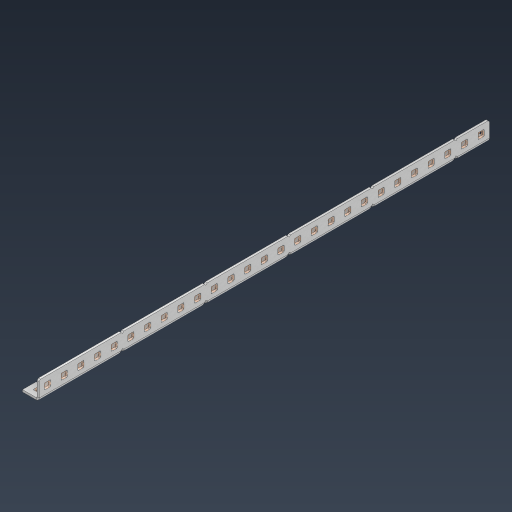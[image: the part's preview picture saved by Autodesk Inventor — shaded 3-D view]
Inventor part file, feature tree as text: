
AUTODESK INVENTOR PART (.ipt)
format: ipt  version: 2024.3 (Build 283343000, 343)  size: 1,052,672 bytes
history: native  units: in
note: dims shown in document units (in); Inventor stores cm internally (conversion verified against a paired STEP export)
features: other x88, extrude x79, sheet_metal_op x11, pattern_linear x2, mirror x1, chamfer x1, sketch x1
ambient origin geometry x8: Origin, YZ Plane, XZ Plane, XY Plane, X Axis, Y Axis, Z Axis, Center Point
bodies: Solid1 (feature_tree), Body (feature_tree)
feature tree (183):
  sheet_metal_op  "Flanges"
  other  "Flange Pattern Plane"
  other  "Flange Pattern Sketch"
  sheet_metal_op  "Flange Pattern"
  sheet_metal_op  "Body Pattern"
  pattern_linear  "Center Pattern"  Spacing1=13.5in  [1 undecoded]
  other  "Arc Length"
  mirror  "Notch Mirror"
  pattern_linear  "Notch Pattern"  Spacing1=0.0625in  [1 undecoded]
  chamfer  "End Chamfer"
  extrude  "Half Cut"  Depth=0.0625in
  other  "Plate1"
  sketch  "Sketch2"  dims[d0=1.0in d1=13.5in d2=0.0625in d3=0.0625in d4=0.0312in d5=0.125in d6=0.0625in d7=0.5in d8=90.0deg d9=0.0312in d10=0.25in d11=0.0625in d12=0.0625in d16=0.182in d17=0.02in d18=0.0625in d19=0.0in d20=0.25in d21=0.25in d38=10.6299in d40=0.5in d41=0.3937in d43=1.0in d46=0.172in d47=1.0in d48=0.0in d49=0.182in d50=0.02in d51=0.25in d52=0.25in d53=0.0625in d54=0.0in d55=0.172in d56=1.0in d57=0.0in d58=0.25in d60=10.6299in d62=0.5in d63=0.3937in d65=0.5in d85=0.1473in d86=0.1782in d88=0.04in d89=0.0625in d90=0.0in d91=0.04in d92=0.0491in d95=2.5in d96=0.04in d97=0.25in d98=45.0deg d99=0.25in d100=0.5in d101=0.0in d102=2.497in d106=0.182in d107=0.02in d108=0.5in d109=0.5in d110=0.0625in d111=0.0in d112=0.172in d113=0.5in d114=0.0in d117=0.5in d118=0.5in d119=0.5in]
  other  "Plate2"
  sheet_metal_op  "Bend1"
  sheet_metal_op  "Corner1"
  other  "Srf1"
  other  "Srf2"
  other  "Srf91"
  sheet_metal_op  "Body Pattern Sketch"
  other  "Srf92"
  other  "Srf786"
  other  "Srf823"
  other  "Srf824"
  other  "Srf825"
  other  "Srf826"
  other  "Srf827"
  other  "Srf828"
  other  "Srf829"
  other  "Srf856"
  other  "Srf857"
  other  "Srf858"
  other  "Srf859"
  other  "Srf860"
  other  "Srf861"
  other  "Srf862"
  other  "Srf889"
  other  "Srf890"
  other  "Srf891"
  other  "Srf892"
  other  "Srf893"
  other  "Srf894"
  other  "Srf895"
  other  "Srf896"
  other  "Srf922"
  other  "Srf923"
  other  "Srf924"
  other  "Srf925"
  other  "Srf926"
  other  "Srf959"
  other  "Srf960"
  other  "Srf961"
  other  "Srf962"
  other  "Srf963"
  other  "Srf996"
  other  "Srf997"
  other  "Srf998"
  other  "Srf999"
  other  "Srf1000"
  other  "Srf1143"
  other  "Srf1144"
  other  "Srf1145"
  other  "Srf1146"
  other  "Srf1147"
  other  "Srf1148"
  other  "Srf1149"
  other  "Srf1150"
  other  "Srf1151"
  other  "Srf1152"
  other  "Srf1153"
  other  "Srf1154"
  other  "Srf1155"
  other  "Srf1199"
  other  "Srf1200"
  other  "Srf1201"
  other  "Srf1202"
  other  "Srf1203"
  other  "Srf1204"
  other  "Srf1205"
  other  "Srf1206"
  other  "Srf1207"
  other  "Srf1208"
  other  "Srf1209"
  other  "Srf1210"
  other  "Srf1211"
  other  "Srf1255"
  other  "Srf1256"
  other  "Srf1257"
  other  "Srf1258"
  other  "Srf1259"
  other  "Srf1260"
  other  "Srf1261"
  other  "Srf1262"
  other  "Srf1263"
  other  "Srf1264"
  other  "Srf1265"
  other  "Srf1266"
  other  "Srf1267"
  sheet_metal_op  "Flange Stamp"
  sheet_metal_op  "Flange Circle"
  sheet_metal_op  "Body Stamp"
  sheet_metal_op  "Body Circle"
  other  "Center Stamp"
  other  "Center Circle"
  sheet_metal_op  "Notch"
  extrude  "ExtrusionSrf2"  Depth=0.0312in
  extrude  "ExtrusionSrf92"  Depth=0.5in
  extrude  "ExtrusionSrf823"  Depth=0.0625in
  extrude  "ExtrusionSrf824"  Depth=0.5in TaperAngle=90.0deg
  extrude  "ExtrusionSrf825"  Depth=0.5in
  extrude  "ExtrusionSrf826"  Depth=0.0625in
  extrude  "ExtrusionSrf827"  Depth=0.0625in
  extrude  "ExtrusionSrf828"  Depth=0.182in
  extrude  "ExtrusionSrf829"  Depth=0.02in
  extrude  "ExtrusionSrf856"  Depth=0.0625in
  extrude  "ExtrusionSrf857"  TaperAngle=0.0deg  [1 undecoded]
  extrude  "ExtrusionSrf858"  Depth=0.5in
  extrude  "ExtrusionSrf859"  Depth=0.5in
  extrude  "ExtrusionSrf860"  Depth=0.5in
  extrude  "ExtrusionSrf861"  Depth=0.5in
  extrude  "ExtrusionSrf862"  Depth=1.0in TaperAngle=0.0deg
  extrude  "ExtrusionSrf889"  Depth=0.182in
  extrude  "ExtrusionSrf890"  Depth=0.02in
  extrude  "ExtrusionSrf891"  Depth=0.5in
  extrude  "ExtrusionSrf892"  Depth=0.5in
  extrude  "ExtrusionSrf893"  Depth=0.0625in
  extrude  "ExtrusionSrf894"  TaperAngle=0.0deg  [1 undecoded]
  extrude  "ExtrusionSrf895"  Depth=0.5in
  extrude  "ExtrusionSrf896"  Depth=1.0in TaperAngle=0.0deg
  extrude  "ExtrusionSrf922"  Depth=0.5in
  extrude  "ExtrusionSrf923"  Depth=0.5in
  extrude  "ExtrusionSrf924"  Depth=0.5in
  extrude  "ExtrusionSrf925"  Depth=0.5in
  extrude  "ExtrusionSrf926"  Depth=0.5in
  extrude  "ExtrusionSrf959"  Depth=0.5in
  extrude  "ExtrusionSrf960"  Depth=0.0625in
  extrude  "ExtrusionSrf961"  TaperAngle=0.0deg  [1 undecoded]
  extrude  "ExtrusionSrf962"  Depth=0.5in
  extrude  "ExtrusionSrf963"  Depth=0.5in
  extrude  "ExtrusionSrf996"  Depth=0.5in
  extrude  "ExtrusionSrf997"  Depth=0.5in TaperAngle=45.0deg
  extrude  "ExtrusionSrf998"  Depth=0.5in
  extrude  "ExtrusionSrf999"  Depth=0.5in TaperAngle=0.0deg
  extrude  "ExtrusionSrf1000"  Depth=0.5in
  extrude  "ExtrusionSrf1143"  Depth=0.182in
  extrude  "ExtrusionSrf1144"  Depth=0.02in
  extrude  "ExtrusionSrf1145"  Depth=0.5in
  extrude  "ExtrusionSrf1146"  Depth=0.5in
  extrude  "ExtrusionSrf1147"  Depth=0.0625in
  extrude  "ExtrusionSrf1148"  TaperAngle=0.0deg  [1 undecoded]
  extrude  "ExtrusionSrf1149"  Depth=0.5in
  extrude  "ExtrusionSrf1150"  Depth=0.5in TaperAngle=0.0deg
  extrude  "ExtrusionSrf1151"  Depth=0.5in
  extrude  "ExtrusionSrf1152"  Depth=0.5in
  extrude  "ExtrusionSrf1153"  Depth=0.5in
  extrude  "ExtrusionSrf1154"  [1 undecoded]
  extrude  "ExtrusionSrf1155"  [1 undecoded]
  extrude  "ExtrusionSrf1199"  [1 undecoded]
  extrude  "ExtrusionSrf1200"  [1 undecoded]
  extrude  "ExtrusionSrf1201"  [1 undecoded]
  extrude  "ExtrusionSrf1202"  [1 undecoded]
  extrude  "ExtrusionSrf1203"  [1 undecoded]
  extrude  "ExtrusionSrf1204"  [1 undecoded]
  extrude  "ExtrusionSrf1205"  [1 undecoded]
  extrude  "ExtrusionSrf1206"  [1 undecoded]
  extrude  "ExtrusionSrf1207"  [1 undecoded]
  extrude  "ExtrusionSrf1208"  [1 undecoded]
  extrude  "ExtrusionSrf1209"  [1 undecoded]
  extrude  "ExtrusionSrf1210"  [1 undecoded]
  extrude  "ExtrusionSrf1211"  [1 undecoded]
  extrude  "ExtrusionSrf1255"  [1 undecoded]
  extrude  "ExtrusionSrf1256"  [1 undecoded]
  extrude  "ExtrusionSrf1257"  [1 undecoded]
  extrude  "ExtrusionSrf1258"  [1 undecoded]
  extrude  "ExtrusionSrf1259"  [1 undecoded]
  extrude  "ExtrusionSrf1260"  [1 undecoded]
  extrude  "ExtrusionSrf1261"  [1 undecoded]
  extrude  "ExtrusionSrf1262"  [1 undecoded]
  extrude  "ExtrusionSrf1263"  [1 undecoded]
  extrude  "ExtrusionSrf1264"  [1 undecoded]
  extrude  "ExtrusionSrf1265"  [1 undecoded]
  extrude  "ExtrusionSrf1266"  [1 undecoded]
  extrude  "ExtrusionSrf1267"  [1 undecoded]
note: 34 required parameter values undecoded (feature->parameter linkage not recoverable at this tier; creation-order binding heuristic only, values carry confidence <= 0.55)
